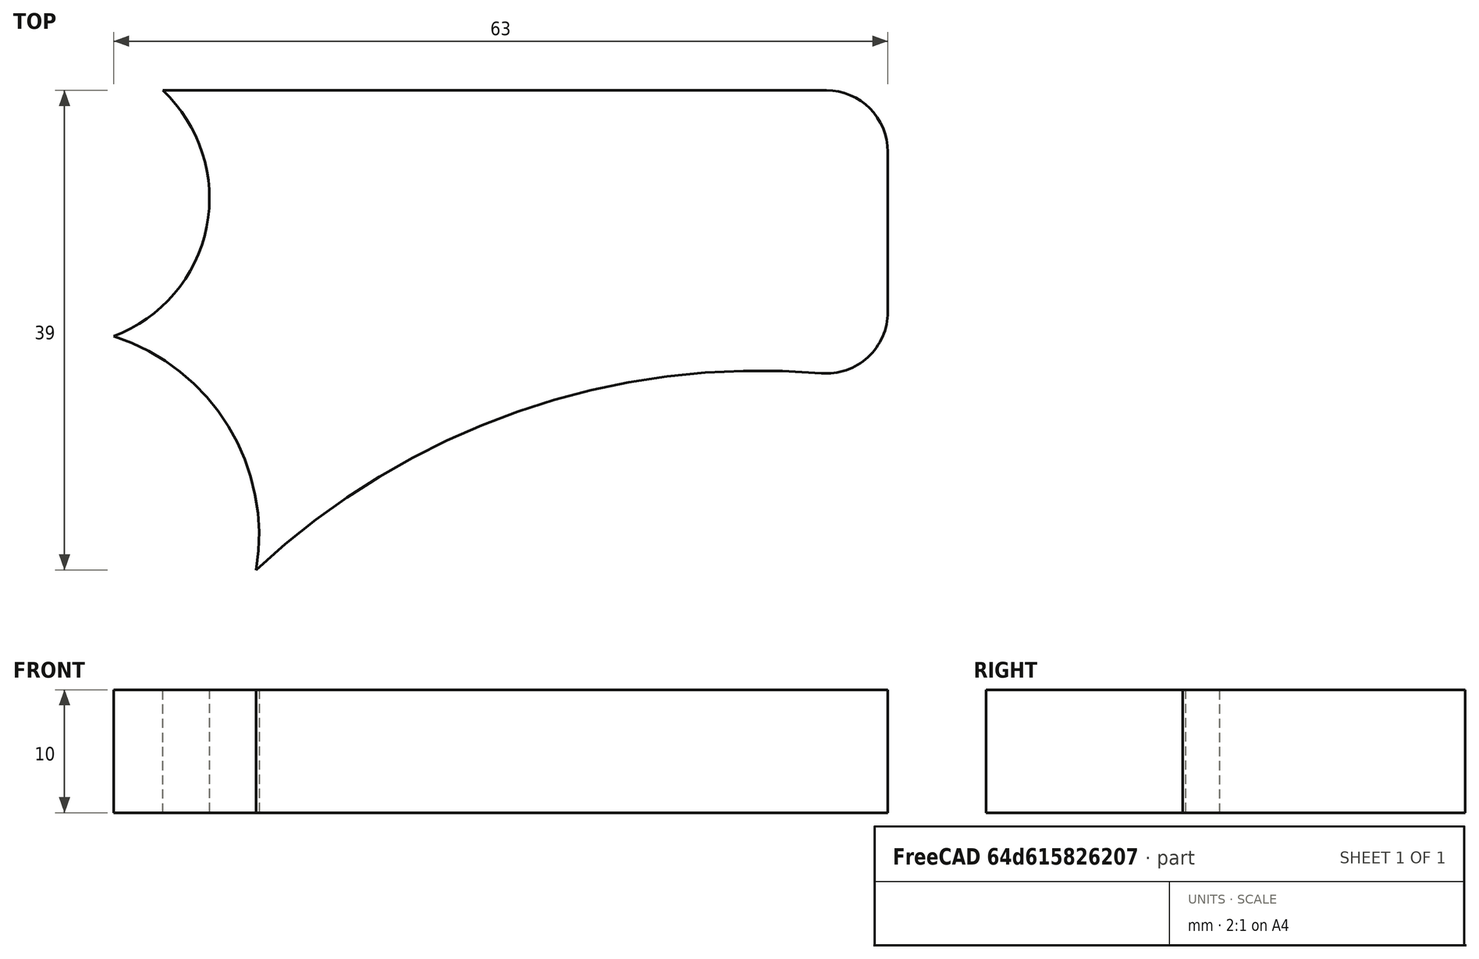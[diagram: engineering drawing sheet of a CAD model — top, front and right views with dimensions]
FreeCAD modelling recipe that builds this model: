
FCSTD DOCUMENT  (FreeCAD 0.19R23756 (Git))
Label: CLAMP_7
License: All rights reserved
LicenseURL: http://en.wikipedia.org/wiki/All_rights_reserved
objects: Sketcher::SketchObject×1, PartDesign::Pad×1, PartDesign::Body×1
note: 4 computed .brp shape members not serialized (recipe doc carries the construction recipe); baked Part::Feature solids carry a one-line shape summary decoded from their .brp

FEATURE [Sketcher::SketchObject] Sketch
  FullyConstrained = true
  MapMode = 5
  Support = -> [XY_Plane]
  sketch-geometry (7):
    g0: LineSegment StartX=0 StartY=1.8e-15 StartZ=0 EndX=54 EndY=0 EndZ=0
    g1: ArcOfCircle CenterX=54 CenterY=-5 CenterZ=0 NormalX=0 NormalY=0 NormalZ=1 AngleXU=0 Radius=5 StartAngle=2e-16 EndAngle=1.5708
    g2: LineSegment StartX=59 StartY=-5 StartZ=0 EndX=59 EndY=-18.0172 EndZ=0
    g3: ArcOfCircle CenterX=54 CenterY=-18.0172 CenterZ=0 NormalX=0 NormalY=0 NormalZ=1 AngleXU=0 Radius=5 StartAngle=4.62943 EndAngle=6.28319
    g4: ArcOfCircle CenterX=48.6136 CenterY=-82.7936 CenterZ=0 NormalX=0 NormalY=0 NormalZ=1 AngleXU=0 Radius=60 StartAngle=1.48783 EndAngle=2.32343
    g5: ArcOfCircle CenterX=-9.16711 CenterY=-36.1957 CenterZ=0 NormalX=0 NormalY=0 NormalZ=1 AngleXU=0 Radius=17 StartAngle=6.11747 EndAngle=7.54515
    g6: ArcOfCircle CenterX=-8.20174 CenterY=-8.75965 CenterZ=0 NormalX=0 NormalY=0 NormalZ=1 AngleXU=0 Radius=12 StartAngle=5.07011 EndAngle=7.10146
  constraints (21):
    c: Coincident(g-1,g0)
    c: PointOnObject(g0,g-1)
    c: Tangent(g0,g1) = 1.5708
    c: Tangent(g1,g2) = 1.5708
    c: Tangent(g2,g3) = 1.5708
    c: Tangent(g3,g4) = 1.5708
    c: Coincident(g5,g4)
    c: Coincident(g6,g5)
    c: Coincident(g6,g0)
    c: Vertical(g2)
    c: DistanceX(g0,g1) = 59
    c: Equal(g1,g3)
    c: Radius(g3) = 5
    c: DistanceX(g4) = 7.6
    c: DistanceY(g4) = -39
    c: DistanceX(g5) = -4
    c: DistanceY(g5) = -20
    c: Radius(g5) = 17
    c: Radius(g6) = 12
    c: DistanceY(g3,g0) = 23
    c: Radius(g4) = 60
FEATURE [PartDesign::Pad] Pad
  AllowMultiFace = false
  Direction = (1,1,1)
  Length = 10
  Length2 = 100
  Profile = -> Sketch
  Type = 0
FEATURE [PartDesign::Body] Body
  Group = -> [Sketch,Pad]
  Origin = -> Origin
  Tip = -> Pad
